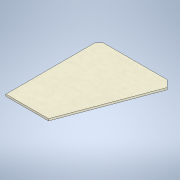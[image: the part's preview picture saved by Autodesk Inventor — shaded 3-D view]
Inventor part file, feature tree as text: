
AUTODESK INVENTOR PART (.ipt)
format: ipt  version: 2021 (Build 250183000, 183)  size: 105,472 bytes
history: native  units: mm
features: extrude x1, sketch x1
ambient origin geometry x8: Origin, YZ Plane, XZ Plane, XY Plane, X Axis, Y Axis, Z Axis, Center Point
bodies: Solid1 (feature_tree)
feature tree (2):
  extrude  "Extrusion1"  Depth=1.7mm
  sketch  "Sketch1"  dims[d0=3.5mm d1=3.5mm d2=81.4mm d3=37.2mm d4=65.5mm d5=59.65mm d6=1.7mm d7=0.0mm]
